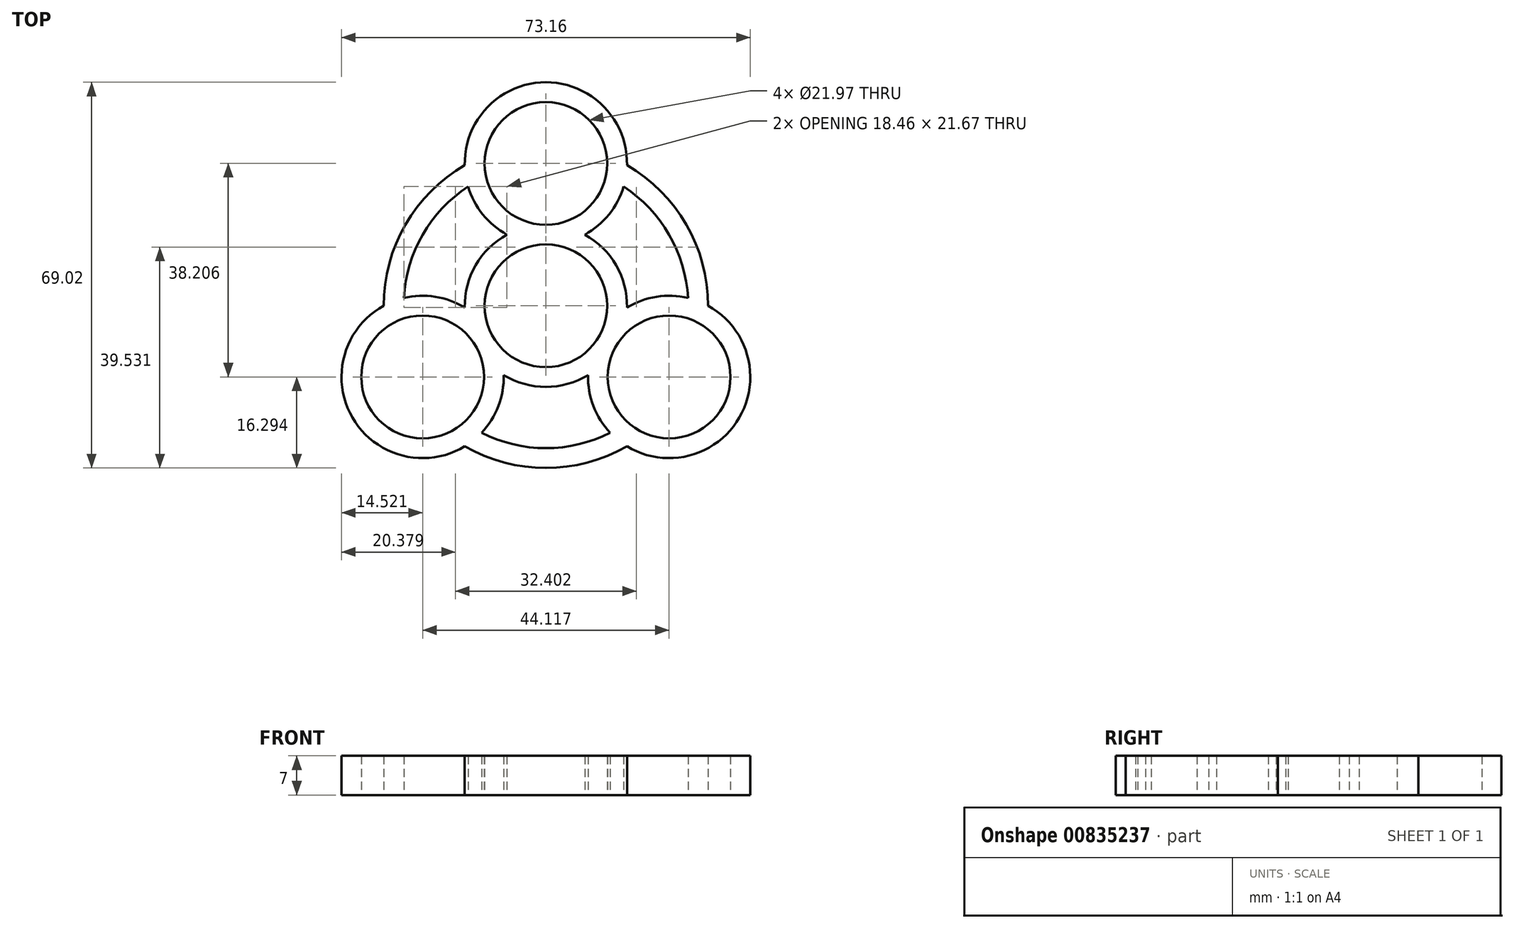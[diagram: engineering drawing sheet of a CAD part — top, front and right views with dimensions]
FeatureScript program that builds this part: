
annotation { "Feature Type Name" : "Feature", "Feature Type Description" : "" }
export const myFeature = defineFeature(function(context is Context, id is Id, definition is map)
    precondition{}
    {
        {
            var Q0;
            Q0=qCreatedBy(makeId("Top.planeOp"),FACE);
            var sketch = newSketch(context, id + "F0", { "sketchPlane" : qUnion([Q0])});
            skCircle(sketch, "E0", {"center": v(0, 0) * mm, "radius": 10.99 * mm});
            skArc(sketch, "E1", {"start": v(10.73, 23.1) * mm, "mid": v(0, 25.47) * mm, "end": v(-10.73, 23.1) * mm, "construction": true});
            skCircle(sketch, "E2", {"center": v(0, 25.47) * mm, "radius": 10.99 * mm});
            skCircle(sketch, "E3", {"center": v(-22.06, -12.74) * mm, "radius": 10.99 * mm});
            skCircle(sketch, "E4", {"center": v(22.06, -12.74) * mm, "radius": 10.99 * mm});
            skLineSegment(sketch, "E5", {"start": v(-22.06, -12.74) * mm, "end": v(7.54, -12.74) * mm, "construction": true});
            skLineSegment(sketch, "E6", {"start": v(0, 25.47) * mm, "end": v(-5.5, 15.96) * mm, "construction": true});
            skLineSegment(sketch, "E7", {"start": v(22.06, -12.74) * mm, "end": v(16.57, -3.22) * mm, "construction": true});
            skLineSegment(sketch, "E8.bottom", {"start": v(-57.15, 57.15) * mm, "end": v(57.15, 57.15) * mm, "construction": true});
            skLineSegment(sketch, "E8.top", {"start": v(-57.15, -57.15) * mm, "end": v(57.15, -57.15) * mm, "construction": true});
            skLineSegment(sketch, "E8.left", {"start": v(-57.15, 57.15) * mm, "end": v(-57.15, -57.15) * mm, "construction": true});
            skLineSegment(sketch, "E8.right", {"start": v(57.15, 57.15) * mm, "end": v(57.15, -57.15) * mm, "construction": true});
            skPoint(sketch, "E9", {"position": v(-57.15, 0) * mm});
            skPoint(sketch, "E10", {"position": v(0, 57.15) * mm});
            skArc(sketch, "E11", {"start": v(14.51, -25.14) * mm, "mid": v(34.63, -20) * mm, "end": v(29.03, 0) * mm});
            skArc(sketch, "E12", {"start": v(-13.92, 21.33) * mm, "mid": v(-11.3, 16.35) * mm, "end": v(-6.97, 12.74) * mm});
            skArc(sketch, "E13", {"start": v(-29.03, 0) * mm, "mid": v(-34.63, -20) * mm, "end": v(-14.51, -25.14) * mm});
            skArc(sketch, "E14", {"start": v(-10.73, 23.1) * mm, "mid": v(-21.1, 14.28) * mm, "end": v(-25.43, 1.38) * mm});
            skArc(sketch, "E15", {"start": v(25.43, 1.38) * mm, "mid": v(22.06, 12.74) * mm, "end": v(13.92, 21.33) * mm});
            skArc(sketch, "E16", {"start": v(-11.52, -22.72) * mm, "mid": v(0, -25.47) * mm, "end": v(11.52, -22.72) * mm});
            skArc(sketch, "E17", {"start": v(-14.51, 25.14) * mm, "mid": v(-25.14, 14.51) * mm, "end": v(-29.03, 0) * mm});
            skArc(sketch, "E18", {"start": v(29.03, 0) * mm, "mid": v(25.14, 14.51) * mm, "end": v(14.51, 25.14) * mm});
            skArc(sketch, "E19", {"start": v(-14.51, -25.14) * mm, "mid": v(0, -29.03) * mm, "end": v(14.51, -25.14) * mm});
            skArc(sketch, "E20", {"start": v(-12.88, -6.7) * mm, "mid": v(-12.57, -7.26) * mm, "end": v(-12.25, -7.8) * mm});
            skLineSegment(sketch, "E21.trimOffspring", {"start": v(-14.51, 0.33) * mm, "end": v(-22.06, -12.74) * mm, "construction": true});
            skArc(sketch, "E22.trimOffspring", {"start": v(-11.52, -22.72) * mm, "mid": v(-8.51, -17.95) * mm, "end": v(-7.55, -12.4) * mm});
            skArc(sketch, "E23.trimOffspring", {"start": v(-9.18, -6.03) * mm, "mid": v(-9.49, -5.48) * mm, "end": v(-9.81, -4.94) * mm});
            skArc(sketch, "E24.trimOffspring", {"start": v(-7.55, -12.4) * mm, "mid": v(0, -14.52) * mm, "end": v(7.55, -12.4) * mm});
            skArc(sketch, "E25.trimOffspring", {"start": v(-14.51, -0.33) * mm, "mid": v(-19.8, 1.6) * mm, "end": v(-25.43, 1.38) * mm});
            skArc(sketch, "E26.trimOffspring", {"start": v(25.43, 1.38) * mm, "mid": v(19.8, 1.6) * mm, "end": v(14.51, -0.33) * mm});
            skLineSegment(sketch, "E27.trimOffspring", {"start": v(11.07, -12.74) * mm, "end": v(22.06, -12.74) * mm, "construction": true});
            skLineSegment(sketch, "E28.trimOffspring", {"start": v(14.8, -0.16) * mm, "end": v(7.26, 12.9) * mm, "construction": true});
            skArc(sketch, "E29.trimOffspring", {"start": v(14.51, -0.33) * mm, "mid": v(12.57, 7.26) * mm, "end": v(6.97, 12.74) * mm});
            skArc(sketch, "E30.trimOffspring", {"start": v(12.25, -7.8) * mm, "mid": v(12.57, -7.26) * mm, "end": v(12.88, -6.7) * mm});
            skArc(sketch, "E31.trimOffspring", {"start": v(9.81, -4.94) * mm, "mid": v(9.49, -5.48) * mm, "end": v(9.18, -6.03) * mm});
            skArc(sketch, "E32.trimOffspring", {"start": v(7.55, -12.4) * mm, "mid": v(8.51, -17.95) * mm, "end": v(11.52, -22.72) * mm});
            skArc(sketch, "E33.trimOffspring", {"start": v(14.51, 25.14) * mm, "mid": v(0, 39.99) * mm, "end": v(-14.51, 25.14) * mm});
            skLineSegment(sketch, "E34.trimOffspring", {"start": v(5.5, 15.96) * mm, "end": v(0, 25.47) * mm, "construction": true});
            skLineSegment(sketch, "E35.trimOffspring", {"start": v(-7.26, 12.9) * mm, "end": v(-7.55, 12.4) * mm, "construction": true});
            skArc(sketch, "E36.trimOffspring", {"start": v(-6.97, 12.74) * mm, "mid": v(-12.57, 7.26) * mm, "end": v(-14.51, -0.33) * mm});
            skArc(sketch, "E37.trimOffspring", {"start": v(0.63, 14.5) * mm, "mid": v(0, 14.52) * mm, "end": v(-0.63, 14.5) * mm});
            skArc(sketch, "E38.trimOffspring", {"start": v(6.97, 12.74) * mm, "mid": v(11.3, 16.35) * mm, "end": v(13.92, 21.33) * mm});
            skArc(sketch, "E39.trimOffspring", {"start": v(-0.63, 10.97) * mm, "mid": v(0, 10.95) * mm, "end": v(0.63, 10.97) * mm});
            skArc(sketch, "E40.trimOffspring", {"start": v(-13.92, 21.33) * mm, "mid": v(0, -25.47) * mm, "end": v(13.92, 21.33) * mm, "construction": true});
            skSolve(sketch);
        }
        {
            var Q0;
            Q0 = qSketchRegion(id + "F0", true);
            extrude(context, id + "F1", {"entities" : qUnion([Q0]), "depth" : 7 * mm, "offsetDistance" : 25.4 * mm});
        }
    });
